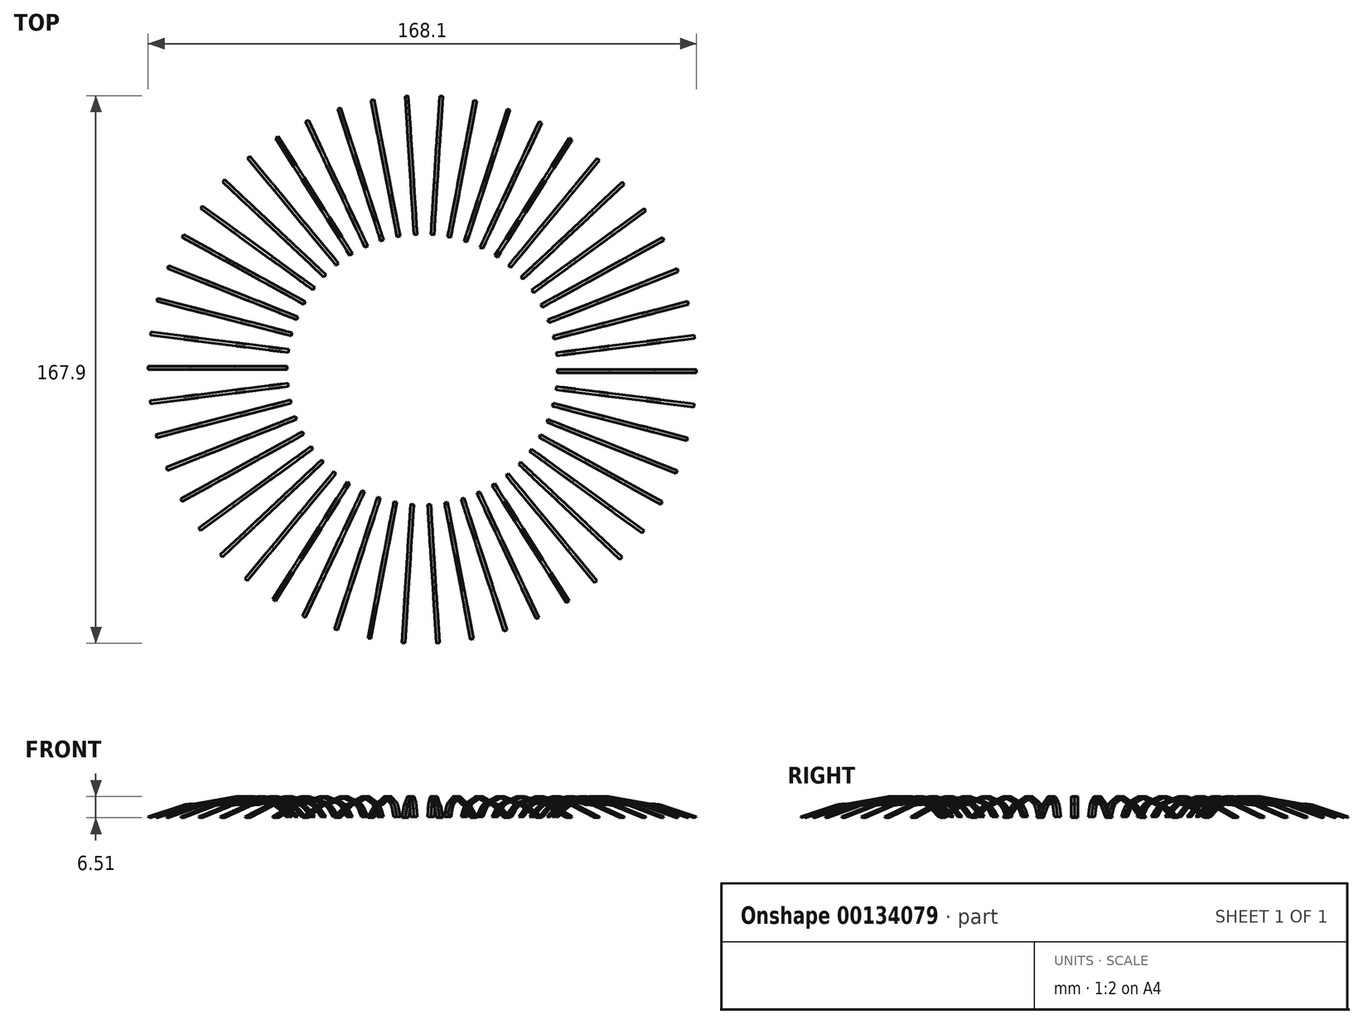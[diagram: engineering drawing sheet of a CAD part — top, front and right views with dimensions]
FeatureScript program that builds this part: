
annotation { "Feature Type Name" : "Feature", "Feature Type Description" : "" }
export const myFeature = defineFeature(function(context is Context, id is Id, definition is map)
    precondition{}
    {
        {
            var Q0;
            Q0=qCreatedBy(makeId("Front.planeOp"),FACE);
            var sketch = newSketch(context, id + "F0", { "sketchPlane" : qUnion([Q0])});
            skLineSegment(sketch, "E0", {"start": v(0, 0) * mm, "end": v(0, -71.97) * mm, "construction": true});
            skSolve(sketch);
        }
        {
            var Q0;
            Q0=qCreatedBy(makeId("Front.planeOp"),FACE);
            var sketch = newSketch(context, id + "F1", { "sketchPlane" : qUnion([Q0])});
            skLineSegment(sketch, "E1", {"start": v(39.66, 0) * mm, "end": v(41.42, 0) * mm});
            skLineSegment(sketch, "E2", {"start": v(41.42, 0) * mm, "end": v(43.34, 2.1) * mm});
            skLineSegment(sketch, "E3", {"start": v(47.49, 4.5) * mm, "end": v(54.59, 6.08) * mm});
            skLineSegment(sketch, "E4", {"start": v(57.76, 6.15) * mm, "end": v(69.21, 4.07) * mm});
            skLineSegment(sketch, "E5", {"start": v(70.64, 3.94) * mm, "end": v(71.15, 3.94) * mm});
            skLineSegment(sketch, "E6", {"start": v(73.73, 3.52) * mm, "end": v(84.05, 0) * mm});
            skPoint(sketch, "E7.visualSharp", {"position": v(72.47, 3.94) * mm});
            skArc(sketch, "E7.filletArc", {"start": v(73.73, 3.52) * mm, "mid": v(72.45, 3.84) * mm, "end": v(71.15, 3.94) * mm});
            skPoint(sketch, "E8.visualSharp", {"position": v(69.92, 3.94) * mm});
            skArc(sketch, "E8.filletArc", {"start": v(69.21, 4.07) * mm, "mid": v(69.92, 3.98) * mm, "end": v(70.64, 3.94) * mm});
            skPoint(sketch, "E9.visualSharp", {"position": v(56.17, 6.44) * mm});
            skArc(sketch, "E9.filletArc", {"start": v(57.76, 6.15) * mm, "mid": v(56.17, 6.27) * mm, "end": v(54.59, 6.08) * mm});
            skPoint(sketch, "E10.visualSharp", {"position": v(45.03, 3.94) * mm});
            skArc(sketch, "E10.filletArc", {"start": v(47.49, 4.5) * mm, "mid": v(45.23, 3.6) * mm, "end": v(43.34, 2.1) * mm});
            skArc(sketch, "E11.0", {"start": v(57.5, 5.94) * mm, "mid": v(56.07, 6.02) * mm, "end": v(54.64, 5.84) * mm});
            skLineSegment(sketch, "E11.1", {"start": v(39.66, -0.25) * mm, "end": v(41.53, -0.25) * mm});
            skLineSegment(sketch, "E11.2", {"start": v(41.53, -0.25) * mm, "end": v(43.52, 1.92) * mm});
            skArc(sketch, "E11.3", {"start": v(47.54, 4.25) * mm, "mid": v(45.35, 3.4) * mm, "end": v(43.52, 1.92) * mm});
            skLineSegment(sketch, "E11.4", {"start": v(47.54, 4.25) * mm, "end": v(54.64, 5.84) * mm});
            skLineSegment(sketch, "E12.0", {"start": v(70.64, 3.7) * mm, "end": v(71.25, 3.7) * mm});
            skArc(sketch, "E12.1", {"start": v(69.17, 3.83) * mm, "mid": v(69.9, 3.73) * mm, "end": v(70.64, 3.7) * mm});
            skLineSegment(sketch, "E12.2", {"start": v(57.97, 5.85) * mm, "end": v(69.17, 3.83) * mm});
            skArc(sketch, "E13.0", {"start": v(73.65, 3.28) * mm, "mid": v(72.47, 3.58) * mm, "end": v(71.27, 3.7) * mm});
            skLineSegment(sketch, "E13.1", {"start": v(73.65, 3.28) * mm, "end": v(83.97, -0.24) * mm});
            skLineSegment(sketch, "E14", {"start": v(39.66, -0.25) * mm, "end": v(39.66, 0) * mm});
            skLineSegment(sketch, "E15", {"start": v(83.97, -0.24) * mm, "end": v(84.05, 0) * mm});
            skLineSegment(sketch, "E16", {"start": v(57.5, 5.94) * mm, "end": v(57.97, 5.85) * mm});
            skLineSegment(sketch, "E17", {"start": v(71.27, 3.7) * mm, "end": v(71.25, 3.7) * mm});
            skSolve(sketch);
        }
        {
            var Q0;
            Q0 = qSketchRegion(id + "F1", true);
            extrude(context, id + "F8", {"entities" : qUnion([Q0]), "depth" : 1 * mm});
        }
        {
            var Q0;
            Q0=makeQuery(id+"F8.opExtrude","SWEPT_BODY",BODY,{"disambiguationData":[OSD([sQuery(id+"F1.wireOp",EDGE,"E1"),sQuery(id+"F1.wireOp",EDGE,"E2"),sQuery(id+"F1.wireOp",EDGE,"E3"),sQuery(id+"F1.wireOp",EDGE,"E4"),sQuery(id+"F1.wireOp",EDGE,"E5"),sQuery(id+"F1.wireOp",EDGE,"E6"),sQuery(id+"F1.wireOp",EDGE,"E7.filletArc"),sQuery(id+"F1.wireOp",EDGE,"E8.filletArc"),sQuery(id+"F1.wireOp",EDGE,"E9.filletArc"),sQuery(id+"F1.wireOp",EDGE,"E10.filletArc"),sQuery(id+"F1.wireOp",EDGE,"E11.0"),sQuery(id+"F1.wireOp",EDGE,"E11.1"),sQuery(id+"F1.wireOp",EDGE,"E11.2"),sQuery(id+"F1.wireOp",EDGE,"E11.3"),sQuery(id+"F1.wireOp",EDGE,"E11.4"),sQuery(id+"F1.wireOp",EDGE,"E12.0"),sQuery(id+"F1.wireOp",EDGE,"E12.1"),sQuery(id+"F1.wireOp",EDGE,"E12.2"),sQuery(id+"F1.wireOp",EDGE,"E13.0"),sQuery(id+"F1.wireOp",EDGE,"E13.1"),sQuery(id+"F1.wireOp",EDGE,"E14"),sQuery(id+"F1.wireOp",EDGE,"E15")])]});
            var Q1;
            Q1=sQuery(id+"F0.wireOp",EDGE,"E0");
            circularPattern(context, id + "F2", {"operationType" : NewBodyOperationType.ADD, "entities" : qUnion([Q0]), "axis" : qUnion([Q1]), "angle" : 360 * degree, "instanceCount" : 50, "equalSpace" : true});
        }
        {
            var Q0;
            Q0=qCreatedBy(makeId("Top.planeOp"),FACE);
            var sketch = newSketch(context, id + "F9", { "sketchPlane" : qUnion([Q0])});
            skCircle(sketch, "E18", {"center": v(0, 0) * mm, "radius": 81.53 * mm});
            skSolve(sketch);
        }
        {
            var Q0;
            Q0 = qSketchRegion(id + "F9", true);
            var Q1;
            Q1=makeQuery(id+"F9.imprint","IMPRINT",FACE,{"disambiguationData":[TD([[makeQuery(id+"F9.imprint","IMPRINT",EDGE,{"derivedFrom":sQuery(id+"F9.wireOp",EDGE,"E18")}),1.0]])]});
            extrude(context, id + "F10", {"entities" : qUnion([Q0, Q1]), "operationType" : NewBodyOperationType.REMOVE, "oppositeDirection" : true, "depth" : 0.5 * mm});
        }
    });
